# Revit family: Dachhalter Gummikeil
name_source: partatom
category: HLS-Bauteile
revit_build: Autodesk Revit 2017 (Build: 20190507_1515(x64)
units: mm (PartAtom-declared; Revit-internal decimal feet)

## family parameters
Basisbauteil = Fläche
Beim Laden mit Abzugskörper schneiden = Nein
Bemaßung runder Anschluss = Durchmesser verwenden
Gemeinsam genutzt = Ja
Raumberechnungspunkt = Nein
Teiletyp = Normal

## types (1)
- Dachhalter Gummikeil
    Artikelnummer = 08197598
    Baustoffklasse = B2
    Breite = 270 mm  [stored 0.885827 ft]
    Breite Platte = 0 mm  [stored 0 ft]
    EAN = 4250928420725
    Fabrikat = MEFA
    Firma = MEFA Befestigungs- und Montagesysteme GmbH
    Gewicht = 1.73 kg
    Höhe 1 = 28 mm
    Höhe 2 = 10 mm
    Kurztext1 = Gummikeil Dachhalter
    Kurztext2 = Gummi 270x270x28 / 10 mm 4 °
    Länge = 270 mm  [stored 0.885827 ft]
    Länge Platte = 0 mm  [stored 0 ft]
    Material = Gummi
    Neigung = 4 °
    Sicherheitsfaktor = 0
    Stärke = 28 mm  [stored 0.0918635 ft]
    Stärke Platte = 0 mm  [stored 0 ft]
    Vorgabe-Ansicht = 1219 mm
    max. Profilhöhe = 0 mm  [stored 0 ft]
    max. zul. Last Druck = 0.90 kip

note: [stored X ft] marks values corroborated as IEEE doubles in the binary element streams (Revit-internal decimal feet)
